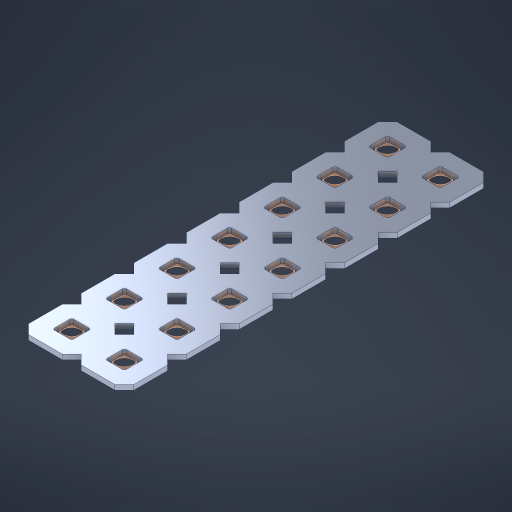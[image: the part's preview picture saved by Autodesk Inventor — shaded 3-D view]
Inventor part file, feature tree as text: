
AUTODESK INVENTOR PART (.ipt)
format: ipt  version: 2023 (Build 270158000, 158)  size: 410,624 bytes
history: native  units: in
note: dims shown in document units (in); Inventor stores cm internally (conversion verified against a paired STEP export)
features: other x15, extrude x13, sketch x2, pattern_linear x1
ambient origin geometry x8: Origin, YZ Plane, XZ Plane, XY Plane, X Axis, Y Axis, Z Axis, Center Point
bodies: Solid1 (feature_tree), Body (feature_tree)
feature tree (31):
  pattern_linear  "Rectangular Pattern1"  Spacing1=0.09in  [1 undecoded]
  sketch  "Sketch1"  dims[d1=0.5in]
  sketch  "Sketch2"  dims[d2=0.182in d3=0.09in d4=0.09in d5=0.09in d6=0.09in d7=0.09in d8=0.09in d9=0.09in d10=0.09in d11=0.02in d13=0.0in d14=0.172in d15=0.0625in d16=0.0in d19=0.5in d22=0.5in]
  other  "Srf1"
  other  "Srf126"
  other  "Srf127"
  other  "Srf128"
  other  "Srf129"
  other  "Srf130"
  other  "Srf131"
  other  "Srf268"
  other  "Srf269"
  other  "Srf270"
  other  "Srf271"
  other  "Srf272"
  other  "Srf273"
  other  "Srf274"
  other  "Circle"
  extrude  "ExtrusionSrf126"  Depth=0.09in
  extrude  "ExtrusionSrf127"  Depth=0.09in
  extrude  "ExtrusionSrf128"  Depth=0.09in
  extrude  "ExtrusionSrf129"  Depth=0.09in
  extrude  "ExtrusionSrf130"  Depth=0.09in
  extrude  "ExtrusionSrf131"  Depth=0.09in
  extrude  "ExtrusionSrf268"  Depth=0.09in
  extrude  "ExtrusionSrf269"  Depth=0.02in
  extrude  "ExtrusionSrf270"  TaperAngle=0.0deg  [1 undecoded]
  extrude  "ExtrusionSrf271"  Depth=0.5in
  extrude  "ExtrusionSrf272"  Depth=0.5in TaperAngle=0.0deg
  extrude  "ExtrusionSrf273"  Depth=0.5in
  extrude  "ExtrusionSrf274"  Depth=0.5in
note: 2 required parameter values undecoded (feature->parameter linkage not recoverable at this tier; creation-order binding heuristic only, values carry confidence <= 0.55)
